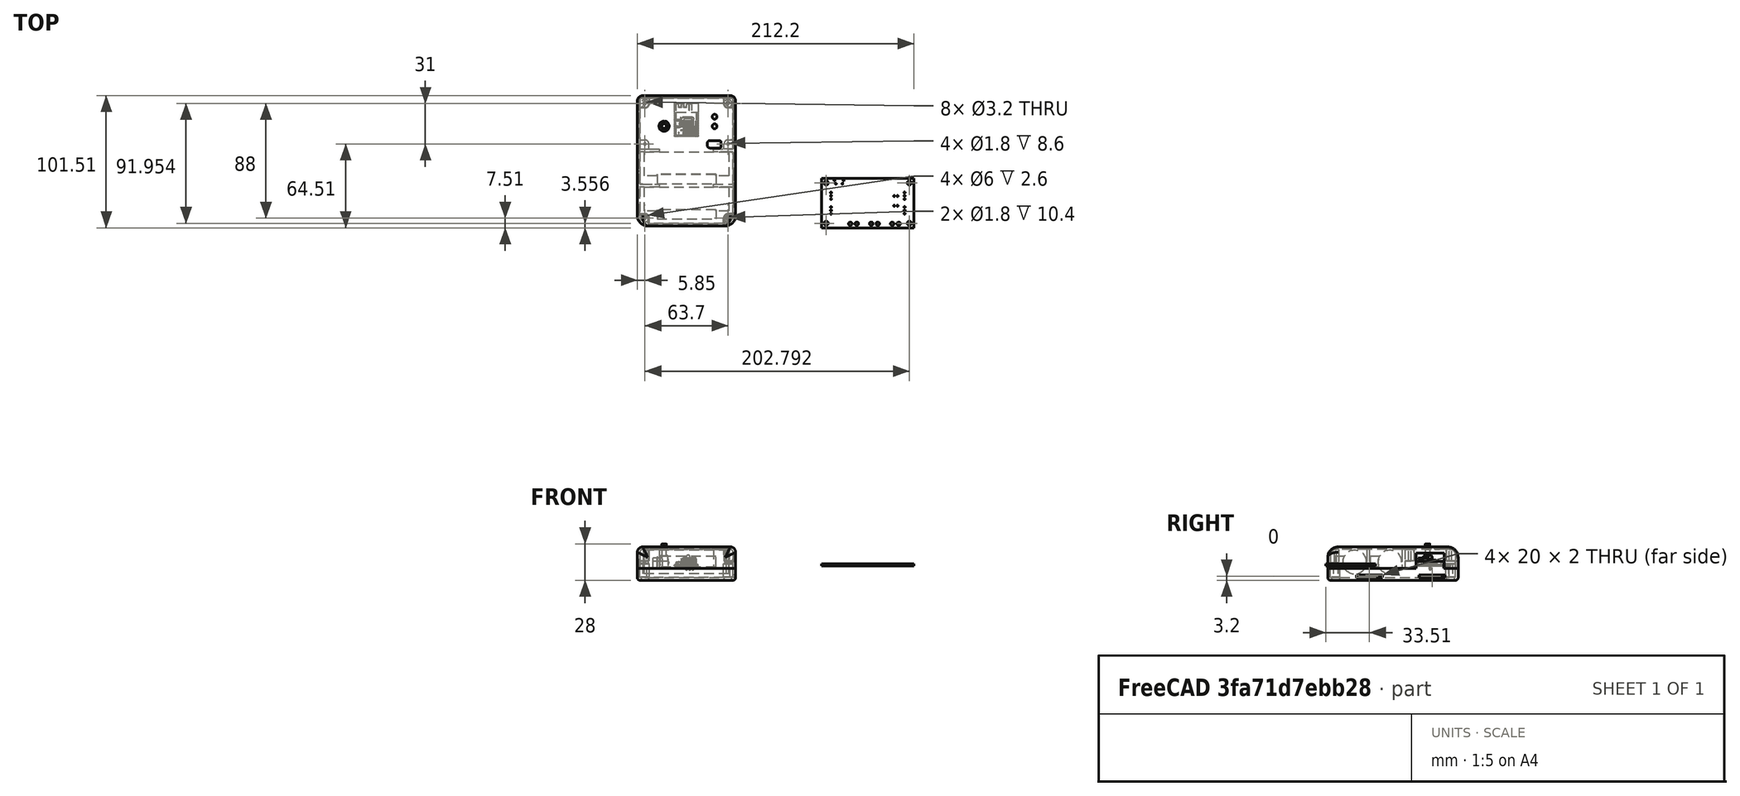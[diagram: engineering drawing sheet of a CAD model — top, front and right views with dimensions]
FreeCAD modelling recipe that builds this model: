
FCSTD DOCUMENT  (FreeCAD 0.21R33694 (Git))
Label: rwled
License: All rights reserved
LicenseURL: http://en.wikipedia.org/wiki/All_rights_reserved
objects: Part::Feature×57, App::Part×44, Sketcher::SketchObject×20, PartDesign::Pad×11, PartDesign::Fillet×11, PartDesign::Pocket×9, PartDesign::Body×4, Part::Part2DObjectPython×1, Mesh::Feature×1, App::DocumentObjectGroup×1
note: 144 computed .brp shape members not serialized (recipe doc carries the construction recipe); baked Part::Feature solids carry a one-line shape summary decoded from their .brp

FEATURE [Part::Feature] Part__Feature  label="SOLID"
  shape: bbox 2 x 1.2 x 0.45 mm, 26 faces (baked)
FEATURE [App::Part] R_0805_2012Metric
  Group = -> [Part__Feature]
  Origin = -> Origin
  Placement = pos=(123.698,-55.352,1.65) rot=(0,0,-1;1.5708rad)
FEATURE [Part::Feature] Part__Feature001  label="SOLID001"
  shape: bbox 7.5 x 4.6 x 2 mm, 40 faces (baked)
FEATURE [App::Part] CP_EIA_7343_20_Kemet_V  label="CP_EIA-7343-20_Kemet-V"
  Group = -> [Part__Feature001]
  Origin = -> Origin045
  Placement = pos=(123.825,-50.8,1.65) rot=(0,0,1;3.14159rad)
FEATURE [Part::Feature] Part__Feature002  label="SOLID002"
  shape: bbox 2.8 x 2.9 x 1.55 mm, 109 faces (baked)
FEATURE [App::Part] SOT_23_5  label="SOT-23-5"
  Group = -> [Part__Feature002]
  Origin = -> Origin046
  Placement = pos=(118.243,-55.372,1.65) rot=(0,0,1;0rad)
FEATURE [Part::Feature] Part__Feature003  label="SOLID003"
  shape: bbox 2 x 2 x 1.05 mm, 118 faces (baked)
FEATURE [App::Part] SOT_363_SC_70_6  label="SOT-363_SC-70-6"
  Group = -> [Part__Feature003]
  Origin = -> Origin047
  Placement = pos=(155.575,-61.468,1.65) rot=(0,0,1;0rad)
FEATURE [Part::Feature] Part__Feature004  label="SOLID004"
  shape: bbox 9.9 x 11.5 x 9.5 mm, 137 faces (baked)
FEATURE [App::Part] JST_XH_S3B_XH_A_1x03_P2_50mm_Horizontal  label="JST_XH_S3B-XH-A_1x03_P2.50mm_Horizontal"
  Group = -> [Part__Feature004]
  Origin = -> Origin048
  Placement = pos=(167.259,-69.048,1.65) rot=(0,0,1;1.5708rad)
FEATURE [Part::Feature] Part__Feature005  label="SOLID005"
  shape: bbox 2 x 1.25 x 1.25 mm, 28 faces (baked)
FEATURE [App::Part] C_0805_2012Metric
  Group = -> [Part__Feature005]
  Origin = -> Origin049
  Placement = pos=(150.368,-55.705,1.65) rot=(0,0,-1;1.5708rad)
FEATURE [Part::Feature] Part__Feature006  label="SOLID006"
  shape: bbox 9.9 x 11.5 x 9.5 mm, 137 faces (baked)
FEATURE [App::Part] JST_XH_S3B_XH_A_1x03_P2_50mm_Horizontal001  label="JST_XH_S3B-XH-A_1x03_P2.50mm_Horizontal001"
  Group = -> [Part__Feature006]
  Origin = -> Origin050
  Placement = pos=(110.892,-64.048,1.65) rot=(0,0,-1;1.5708rad)
FEATURE [Part::Feature] Part__Feature007  label="SOLID007"
  shape: bbox 2 x 1.25 x 1.25 mm, 28 faces (baked)
FEATURE [App::Part] C_0805_2012Metric001
  Group = -> [Part__Feature007]
  Origin = -> Origin051
  Placement = pos=(128.016,-55.372,1.65) rot=(0,0,-1;1.5708rad)
FEATURE [Part::Feature] Part__Feature008  label="SOLID008"
  shape: bbox 18 x 25.5 x 3.1 mm, 751 faces (baked)
FEATURE [App::Part] ESP32_WROOM_32  label="ESP32-WROOM-32"
  Group = -> [Part__Feature008]
  Origin = -> Origin052
  Placement = pos=(139.237,-57.805,1.65) rot=(0,0,1;0rad)
FEATURE [Part::Feature] Part__Feature009  label="SOLID009"
  shape: bbox 2.5 x 2 x 0.78 mm, 48 faces (baked)
FEATURE [App::Part] Bosch_LGA_8_2x2_5mm_P0_65mm_ClockwisePinNumbering  label="Bosch_LGA-8_2x2.5mm_P0.65mm_ClockwisePinNumbering"
  Group = -> [Part__Feature009]
  Origin = -> Origin053
  Placement = pos=(154.394,-55.667,1.65) rot=(0,0,-1;1.5708rad)
FEATURE [Part::Feature] Part__Feature010  label="SOLID010"
  shape: bbox 3.4 x 3.8 x 10.8 mm, 16 faces (baked)
FEATURE [App::Part] LED_D3_0mm  label="LED_D3.0mm"
  Group = -> [Part__Feature010]
  Origin = -> Origin054
  Placement = pos=(159.385,-55.6006,1.65) rot=(0,0,1;0rad)
FEATURE [Part::Feature] Part__Feature011  label="SOLID011"
  shape: bbox 9.9 x 11.5 x 9.5 mm, 137 faces (baked)
FEATURE [App::Part] JST_XH_S3B_XH_A_1x03_P2_50mm_Horizontal002  label="JST_XH_S3B-XH-A_1x03_P2.50mm_Horizontal002"
  Group = -> [Part__Feature011]
  Origin = -> Origin055
  Placement = pos=(167.259,-57.86,1.65) rot=(0,0,1;1.5708rad)
FEATURE [Part::Feature] Part__Feature012  label="SOLID012"
  shape: bbox 2 x 1.25 x 1.25 mm, 28 faces (baked)
FEATURE [App::Part] C_0805_2012Metric002
  Group = -> [Part__Feature012]
  Origin = -> Origin056
  Placement = pos=(121.539,-55.372,1.65) rot=(0,0,-1;1.5708rad)
FEATURE [Part::Feature] Part__Feature013  label="SOLID013"
  shape: bbox 9.9 x 11.5 x 9.5 mm, 137 faces (baked)
FEATURE [App::Part] JST_XH_S3B_XH_A_1x03_P2_50mm_Horizontal003  label="JST_XH_S3B-XH-A_1x03_P2.50mm_Horizontal003"
  Group = -> [Part__Feature013]
  Origin = -> Origin057
  Placement = pos=(110.892,-52.86,1.65) rot=(0,0,-1;1.5708rad)
FEATURE [Part::Feature] Part__Feature014  label="SOLID014"
  shape: bbox 3.4 x 3.8 x 10.8 mm, 16 faces (baked)
FEATURE [App::Part] LED_D3_0mm001  label="LED_D3.0mm001"
  Group = -> [Part__Feature014]
  Origin = -> Origin058
  Placement = pos=(159.385,-62.9901,1.65) rot=(0,0,1;0rad)
FEATURE [Part::Feature] Part__Feature015  label="SOLID015"
  shape: bbox 3.2 x 1.6 x 0.55 mm, 26 faces (baked)
FEATURE [App::Part] R_1206_3216Metric
  Group = -> [Part__Feature015]
  Origin = -> Origin059
  Placement = pos=(160.579,-59.4595,1.65) rot=(0,0,1;0rad)
FEATURE [Part::Feature] Part__Feature016  label="SOLID016"
  shape: bbox 2 x 1.25 x 1.25 mm, 28 faces (baked)
FEATURE [App::Part] C_0805_2012Metric003
  Group = -> [Part__Feature016]
  Origin = -> Origin060
  Placement = pos=(119.507,-58.293,1.65) rot=(0,0,1;0rad)
FEATURE [Part::Feature] Part__Feature017  label="SOLID017"
  shape: bbox 2 x 1.2 x 0.45 mm, 26 faces (baked)
FEATURE [App::Part] R_0805_2012Metric001
  Group = -> [Part__Feature017]
  Origin = -> Origin061
  Placement = pos=(125.862,-55.352,1.65) rot=(0,0,-1;1.5708rad)
FEATURE [Part::Feature] Part__Feature018  label="SOLID018"
  shape: bbox 3.2 x 1.6 x 0.55 mm, 26 faces (baked)
FEATURE [App::Part] R_1206_3216Metric001
  Group = -> [Part__Feature018]
  Origin = -> Origin062
  Placement = pos=(160.579,-52.07,1.65) rot=(0,0,1;0rad)
FEATURE [Part::Feature] Part__Feature019  label="SOLID019"
  shape: bbox 2 x 1.2 x 0.45 mm, 26 faces (baked)
FEATURE [App::Part] R_0805_2012Metric002
  Group = -> [Part__Feature019]
  Origin = -> Origin063
  Placement = pos=(136.779,-52.324,-0.05) rot=(0.707107,-0.707107,0;3.14159rad)
FEATURE [Part::Feature] Part__Feature020  label="SOLID020"
  shape: bbox 2 x 1.2 x 0.45 mm, 26 faces (baked)
FEATURE [App::Part] R_0805_2012Metric003
  Group = -> [Part__Feature020]
  Origin = -> Origin064
  Placement = pos=(128.88,-57.967,-0.05) rot=(0.707107,-0.707107,0;3.14159rad)
FEATURE [Part::Feature] Part__Feature021  label="SOLID021"
  shape: bbox 4 x 4 x 0.77 mm, 158 faces (baked)
FEATURE [App::Part] QFN_24_1EP_4x4mm_P0_5mm_EP2_6x2_6mm  label="QFN-24-1EP_4x4mm_P0.5mm_EP2.6x2.6mm"
  Group = -> [Part__Feature021]
  Origin = -> Origin065
  Placement = pos=(126.397,-49.042,-0.05) rot=(1,0,0;3.14159rad)
FEATURE [Part::Feature] Part__Feature022  label="SOLID022"
  shape: bbox 5 x 2.7 x 2.22 mm, 41 faces (baked)
FEATURE [App::Part] D_SMA
  Group = -> [Part__Feature022]
  Origin = -> Origin066
  Placement = pos=(155.467,-71.628,-0.05) rot=(1,0,0;3.14159rad)
FEATURE [Part::Feature] Part__Feature023  label="SOLID023"
  shape: bbox 5 x 2.7 x 2.22 mm, 41 faces (baked)
FEATURE [App::Part] D_SMA001
  Group = -> [Part__Feature023]
  Origin = -> Origin067
  Placement = pos=(132.62,-71.628,-0.05) rot=(1,0,0;3.14159rad)
FEATURE [Part::Feature] Part__Feature024  label="SOLID024"
  shape: bbox 2.5 x 1.25 x 1.1 mm, 67 faces (baked)
FEATURE [App::Part] D_SOD_323  label="D_SOD-323"
  Group = -> [Part__Feature024]
  Origin = -> Origin068
  Placement = pos=(121.869,-55.1348,-0.05) rot=(0.707107,-0.707107,0;3.14159rad)
FEATURE [Part::Feature] Part__Feature025  label="SOLID025"
  shape: bbox 2 x 1.2 x 0.45 mm, 26 faces (baked)
FEATURE [App::Part] R_0805_2012Metric004
  Group = -> [Part__Feature025]
  Origin = -> Origin069
  Placement = pos=(132.612,-45.593,-0.05) rot=(0,1,0;3.14159rad)
FEATURE [Part::Feature] Part__Feature026  label="COMPOUND"
  shape: bbox 9.25 x 10 x 4.4 mm, 13 faces (baked)
FEATURE [Part::Feature] Part__Feature027  label="COMPOUND001"
  shape: bbox 7.55 x 10 x 1.27 mm, 12 faces (baked)
FEATURE [Part::Feature] Part__Feature028  label="COMPOUND002"
  shape: bbox 4.95 x 1.24 x 2.95 mm, 22 faces (baked)
FEATURE [Part::Feature] Part__Feature029  label="COMPOUND003"
  shape: bbox 1.3 x 1.24 x 0.5 mm, 10 faces (baked)
FEATURE [Part::Feature] Part__Feature030  label="COMPOUND004"
  shape: bbox 4.95 x 1.24 x 2.95 mm, 22 faces (baked)
FEATURE [App::Part] COMPOUND  label="COMPOUND005"
  Group = -> [Part__Feature026,Part__Feature027,Part__Feature028,Part__Feature029,Part__Feature030]
  Origin = -> Origin070
FEATURE [App::Part] TO_263_2  label="TO-263-2"
  Group = -> [COMPOUND]
  Origin = -> Origin071
  Placement = pos=(144.164,-67.195,-0.05) rot=(0.707107,-0.707107,0;3.14159rad)
FEATURE [Part::Feature] Part__Feature031  label="SOLID026"
  shape: bbox 2 x 1.25 x 1.25 mm, 28 faces (baked)
FEATURE [App::Part] C_0805_2012Metric004
  Group = -> [Part__Feature031]
  Origin = -> Origin072
  Placement = pos=(136.398,-66.421,-0.05) rot=(1,0,0;3.14159rad)
FEATURE [Part::Feature] Part__Feature032  label="SOLID027"
  shape: bbox 2 x 1.2 x 0.45 mm, 26 faces (baked)
FEATURE [App::Part] R_0805_2012Metric005
  Group = -> [Part__Feature032]
  Origin = -> Origin073
  Placement = pos=(125.476,-44.577,-0.05) rot=(0,1,0;3.14159rad)
FEATURE [Part::Feature] Part__Feature033  label="SOLID028"
  shape: bbox 2.5 x 1.25 x 1.1 mm, 67 faces (baked)
FEATURE [App::Part] D_SOD_324  label="D_SOD-324"
  Group = -> [Part__Feature033]
  Origin = -> Origin074
  Placement = pos=(120.853,-50.673,-0.05) rot=(0,1,0;3.14159rad)
FEATURE [Part::Feature] Part__Feature034  label="SOLID029"
  shape: bbox 2 x 1.25 x 1.25 mm, 28 faces (baked)
FEATURE [App::Part] C_0805_2012Metric005
  Group = -> [Part__Feature034]
  Origin = -> Origin075
  Placement = pos=(115.824,-51.562,-0.05) rot=(0.707107,-0.707107,0;3.14159rad)
FEATURE [Part::Feature] Part__Feature035  label="SOLID030"
  shape: bbox 2 x 2 x 1.05 mm, 118 faces (baked)
FEATURE [App::Part] SOT_363_SC_70_007  label="SOT-363_SC-70-007"
  Group = -> [Part__Feature035]
  Origin = -> Origin076
  Placement = pos=(133.858,-57.9905,-0.05) rot=(0.707107,-0.707107,0;3.14159rad)
FEATURE [Part::Feature] Part__Feature036  label="SOLID031"
  shape: bbox 2 x 1.2 x 0.45 mm, 26 faces (baked)
FEATURE [App::Part] R_0805_2012Metric006
  Group = -> [Part__Feature036]
  Origin = -> Origin077
  Placement = pos=(142.543,-55.2196,-0.05) rot=(1,0,0;3.14159rad)
FEATURE [Part::Feature] Part__Feature037  label="SOLID032"
  shape: bbox 2 x 1.25 x 1.25 mm, 28 faces (baked)
FEATURE [App::Part] C_0805_2012Metric006
  Group = -> [Part__Feature037]
  Origin = -> Origin078
  Placement = pos=(116.713,-75.504,-0.05) rot=(0.707107,-0.707107,0;3.14159rad)
FEATURE [Part::Feature] Part__Feature038  label="COMPOUND006"
  shape: bbox 9.25 x 10 x 4.4 mm, 13 faces (baked)
FEATURE [Part::Feature] Part__Feature039  label="COMPOUND007"
  shape: bbox 7.55 x 10 x 1.27 mm, 12 faces (baked)
FEATURE [Part::Feature] Part__Feature040  label="COMPOUND008"
  shape: bbox 4.95 x 1.24 x 2.95 mm, 22 faces (baked)
FEATURE [Part::Feature] Part__Feature041  label="COMPOUND009"
  shape: bbox 1.3 x 1.24 x 0.5 mm, 10 faces (baked)
FEATURE [Part::Feature] Part__Feature042  label="COMPOUND010"
  shape: bbox 4.95 x 1.24 x 2.95 mm, 22 faces (baked)
FEATURE [App::Part] COMPOUND001  label="COMPOUND011"
  Group = -> [Part__Feature038,Part__Feature039,Part__Feature040,Part__Feature041,Part__Feature042]
  Origin = -> Origin079
FEATURE [App::Part] TO_263_003  label="TO-263-003"
  Group = -> [COMPOUND001]
  Origin = -> Origin080
  Placement = pos=(121.304,-67.195,-0.05) rot=(0.707107,-0.707107,0;3.14159rad)
FEATURE [Part::Feature] Part__Feature043  label="SOLID033"
  shape: bbox 2 x 1.2 x 0.45 mm, 26 faces (baked)
FEATURE [App::Part] R_0805_2012Metric007
  Group = -> [Part__Feature043]
  Origin = -> Origin081
  Placement = pos=(133.924,-61.214,-0.05) rot=(0,1,0;3.14159rad)
FEATURE [Part::Feature] Part__Feature044  label="SOLID034"
  shape: bbox 2 x 2 x 1.05 mm, 118 faces (baked)
FEATURE [App::Part] SOT_363_SC_70_008  label="SOT-363_SC-70-008"
  Group = -> [Part__Feature044]
  Origin = -> Origin082
  Placement = pos=(132.522,-52.593,-0.05) rot=(0,1,0;3.14159rad)
FEATURE [Part::Feature] Part__Feature045  label="SOLID035"
  shape: bbox 2 x 1.2 x 0.45 mm, 26 faces (baked)
FEATURE [App::Part] R_0805_2012Metric008
  Group = -> [Part__Feature045]
  Origin = -> Origin083
  Placement = pos=(132.612,-49.911,-0.05) rot=(0,1,0;3.14159rad)
FEATURE [Part::Feature] Part__Feature046  label="SOLID036"
  shape: bbox 2.5 x 1.25 x 1.1 mm, 67 faces (baked)
FEATURE [App::Part] D_SOD_325  label="D_SOD-325"
  Group = -> [Part__Feature046]
  Origin = -> Origin084
  Placement = pos=(142.636,-52.8066,-0.05) rot=(1,0,0;3.14159rad)
FEATURE [Part::Feature] Part__Feature047  label="SOLID037"
  shape: bbox 2 x 1.2 x 0.45 mm, 26 faces (baked)
FEATURE [App::Part] R_0805_2012Metric009
  Group = -> [Part__Feature047]
  Origin = -> Origin085
  Placement = pos=(132.612,-47.879,-0.05) rot=(0,1,0;3.14159rad)
FEATURE [Part::Feature] Part__Feature048  label="rwled-ctrl PCB"
  shape: bbox 70.87 x 38.1 x 1.6 mm, 74 faces (baked)
FEATURE [App::Part] rwled_ctrl_1  label="rwled-ctrl 1"
  Group = -> [R_0805_2012Metric,CP_EIA_7343_20_Kemet_V,SOT_23_5,SOT_363_SC_70_6,JST_XH_S3B_XH_A_1x03_P2_50mm_Horizontal,C_0805_2012Metric,JST_XH_S3B_XH_A_1x03_P2_50mm_Horizontal001,C_0805_2012Metric001,ESP32_WROOM_32,Bosch_LGA_8_2x2_5mm_P0_65mm_ClockwisePinNumbering,LED_D3_0mm,JST_XH_S3B_XH_A_1x03_P2_50mm_Horizontal002,C_0805_2012Metric002,JST_XH_S3B_XH_A_1x03_P2_50mm_Horizontal003,LED_D3_0mm001,+26 more]
  Origin = -> Origin086
  Placement = pos=(-139.065,60.96,2) rot=(0,0,1;0rad)
FEATURE [Sketcher::SketchObject] Sketch
  FullyConstrained = true
  MapMode = 5
  Support = -> [XY_Plane043]
  sketch-geometry (4):
    g0: LineSegment StartX=-37.7 StartY=21.5 StartZ=0 EndX=37.7 EndY=21.5 EndZ=0
    g1: LineSegment StartX=37.7 StartY=21.5 StartZ=0 EndX=37.7 EndY=-78.5 EndZ=0
    g2: LineSegment StartX=37.7 StartY=-78.5 StartZ=0 EndX=-37.7 EndY=-78.5 EndZ=0
    g3: LineSegment StartX=-37.7 StartY=-78.5 StartZ=0 EndX=-37.7 EndY=21.5 EndZ=0
  constraints (11):
    c: Coincident(g0,g1)
    c: Coincident(g1,g2)
    c: Coincident(g2,g3)
    c: Coincident(g3,g0)
    c: Horizontal(g2)
    c: Vertical(g1)
    c: Vertical(g3)
    c: Symmetric(g0,g0,g-2)
    c: Distance(g0) = 75.4
    c: Distance(g0,g-1) = 21.5
    c: DistanceY(g3,g3) = 100
FEATURE [Part::Feature] Part__Feature049  label="Micro USB-B Female 5Pin SMD"
  shape: bbox 0.3 x 1.55 x 4.2 mm, 15 faces (baked)
FEATURE [Part::Feature] Part__Feature050  label="Micro USB-B Female 5Pin SMD001"
  shape: bbox 0.3 x 1.55 x 4.2 mm, 15 faces (baked)
FEATURE [Part::Feature] Part__Feature051  label="Micro USB-B Female 5Pin SMD002"
  shape: bbox 0.3 x 1.55 x 4.2 mm, 15 faces (baked)
FEATURE [Part::Feature] Part__Feature052  label="Micro USB-B Female 5Pin SMD003"
  shape: bbox 0.3 x 1.55 x 4.2 mm, 15 faces (baked)
FEATURE [Part::Feature] Part__Feature053  label="Micro USB-B Female 5Pin SMD004"
  shape: bbox 0.3 x 1.55 x 4.2 mm, 15 faces (baked)
FEATURE [Part::Feature] Part__Feature054  label="Micro USB-B Female 5Pin SMD005"
  shape: bbox 6.9 x 2.4 x 4.15 mm, 176 faces (baked)
FEATURE [Part::Feature] Part__Feature055  label="Micro USB-B Female 5Pin SMD006"
  shape: bbox 8.172 x 3.786 x 5.619 mm, 257 faces (baked)
FEATURE [App::Part] Micro_USB_B_Female_5Pin_SMD  label="Micro USB-B Female 5Pin SMD007"
  Group = -> [Part__Feature049,Part__Feature050,Part__Feature051,Part__Feature052,Part__Feature053,Part__Feature054,Part__Feature055]
  Origin = -> Origin087
  Placement = pos=(-22,14.6,4.85) rot=(0,1,1;3.14159rad)
FEATURE [Part::Feature] Part__Feature056  label="SW_PUSH_6mm_h13mm"
  Placement = pos=(-20.29,0.35,4) rot=(0,0,1;0rad)
  shape: bbox 7.174 x 6 x 16.5 mm, 105 faces (baked)
FEATURE [PartDesign::Pad] Pad
  Direction = (0,0,1)
  Length = 16.6
  Length2 = 10
  Profile = -> Sketch
  ReferenceAxis = -> Sketch [N_Axis]
  Type = 0
FEATURE [Sketcher::SketchObject] Sketch001
  FullyConstrained = true
  MapMode = 5
  Placement = pos=(0,0,0) rot=(0.57735,0.57735,0.57735;2.0944rad)
  Support = -> [YZ_Plane088]
  sketch-geometry (1):
    g0: Circle CenterX=9.1 CenterY=0 CenterZ=0 NormalX=0 NormalY=0 NormalZ=1 AngleXU=0 Radius=9.1
  constraints (3):
    c: PointOnObject(g0,g-1)
    c: Distance(g-1,g0) = 9.1
    c: PointOnObject(g-1,g0)
FEATURE [PartDesign::Pad] Pad001
  Direction = (1,-2e-16,3e-16)
  Length = 65
  Length2 = 10
  Placement = pos=(0,0,0) rot=(0.57735,0.57735,0.57735;2.0944rad)
  Profile = -> Sketch001
  ReferenceAxis = -> Sketch001 [N_Axis]
  Type = 0
FEATURE [Sketcher::SketchObject] Sketch002
  FullyConstrained = false
  MapMode = 5
  Placement = pos=(0,0,0) rot=(1,0,0;1.5708rad)
  Support = -> [XZ_Plane088]
  sketch-geometry (4):
    g0: LineSegment StartX=10 StartY=-3.77048 StartZ=0 EndX=55 EndY=-3.77048 EndZ=0
    g1: LineSegment StartX=55 StartY=-3.77048 StartZ=0 EndX=55 EndY=4.22952 EndZ=0
    g2: LineSegment StartX=55 StartY=4.22952 StartZ=0 EndX=10 EndY=4.22952 EndZ=0
    g3: LineSegment StartX=10 StartY=4.22952 StartZ=0 EndX=10 EndY=-3.77048 EndZ=0
  constraints (11):
    c: Coincident(g0,g1)
    c: Coincident(g1,g2)
    c: Coincident(g2,g3)
    c: Coincident(g3,g0)
    c: Horizontal(g0)
    c: Horizontal(g2)
    c: Vertical(g1)
    c: Vertical(g3)
    c: DistanceX(g-1,g0) = 10
    c: DistanceX(g2,g2) = 45
    c: DistanceY(g3,g3) = 8
FEATURE [PartDesign::Pad] Pad002
  BaseFeature = -> Pad001
  Direction = (0,-1,2e-16)
  Length = 6
  Length2 = 10
  Placement = pos=(0,0,0) rot=(0.57735,0.57735,0.57735;2.0944rad)
  Profile = -> Sketch002
  ReferenceAxis = -> Sketch002 [N_Axis]
  Type = 4
FEATURE [PartDesign::Body] Body001  label="accum-a"
  Group = -> [Sketch001,Pad001,Sketch002,Pad002]
  Origin = -> Origin088
  Placement = pos=(-32.5,-40,3) rot=(0,0,1;0rad)
  Tip = -> Pad002
FEATURE [Sketcher::SketchObject] Sketch003
  FullyConstrained = true
  MapMode = 5
  Placement = pos=(0,0,0) rot=(0.57735,0.57735,0.57735;2.0944rad)
  Support = -> [YZ_Plane090]
  sketch-geometry (1):
    g0: Circle CenterX=9.1 CenterY=0 CenterZ=0 NormalX=0 NormalY=0 NormalZ=1 AngleXU=0 Radius=9.1
  constraints (3):
    c: PointOnObject(g0,g-1)
    c: Distance(g-1,g0) = 9.1
    c: PointOnObject(g-1,g0)
FEATURE [PartDesign::Pad] Pad003
  Direction = (1,-2e-16,3e-16)
  Length = 65
  Length2 = 10
  Placement = pos=(0,0,0) rot=(0.57735,0.57735,0.57735;2.0944rad)
  Profile = -> Sketch003
  ReferenceAxis = -> Sketch003 [N_Axis]
  Type = 0
FEATURE [Sketcher::SketchObject] Sketch004
  FullyConstrained = false
  MapMode = 5
  Placement = pos=(0,0,0) rot=(1,0,0;1.5708rad)
  Support = -> [XZ_Plane090]
  sketch-geometry (4):
    g0: LineSegment StartX=10 StartY=-3.77048 StartZ=0 EndX=55 EndY=-3.77048 EndZ=0
    g1: LineSegment StartX=55 StartY=-3.77048 StartZ=0 EndX=55 EndY=4.22952 EndZ=0
    g2: LineSegment StartX=55 StartY=4.22952 StartZ=0 EndX=10 EndY=4.22952 EndZ=0
    g3: LineSegment StartX=10 StartY=4.22952 StartZ=0 EndX=10 EndY=-3.77048 EndZ=0
  constraints (11):
    c: Coincident(g0,g1)
    c: Coincident(g1,g2)
    c: Coincident(g2,g3)
    c: Coincident(g3,g0)
    c: Horizontal(g0)
    c: Horizontal(g2)
    c: Vertical(g1)
    c: Vertical(g3)
    c: DistanceX(g-1,g0) = 10
    c: DistanceX(g2,g2) = 45
    c: DistanceY(g3,g3) = 8
FEATURE [PartDesign::Pad] Pad004
  BaseFeature = -> Pad003
  Direction = (0,-1,2e-16)
  Length = 6
  Length2 = 10
  Placement = pos=(0,0,0) rot=(0.57735,0.57735,0.57735;2.0944rad)
  Profile = -> Sketch004
  ReferenceAxis = -> Sketch004 [N_Axis]
  Type = 4
FEATURE [PartDesign::Body] Body003  label="accum-b"
  Group = -> [Sketch003,Pad003,Sketch004,Pad004]
  Origin = -> Origin090
  Placement = pos=(-32.5,-67,3) rot=(0,0,1;0rad)
  Tip = -> Pad004
FEATURE [Sketcher::SketchObject] Sketch005
  ExternalGeometry = -> [Pad]
  FullyConstrained = true
  MapMode = 5
  Placement = pos=(0,0,0) rot=(1,0,0;3.14159rad)
  Support = -> [Pad]
  sketch-geometry (4):
    g0: LineSegment StartX=-35.7 StartY=76.5 StartZ=0 EndX=35.7 EndY=76.5 EndZ=0
    g1: LineSegment StartX=35.7 StartY=76.5 StartZ=0 EndX=35.7 EndY=-19.5 EndZ=0
    g2: LineSegment StartX=35.7 StartY=-19.5 StartZ=0 EndX=-35.7 EndY=-19.5 EndZ=0
    g3: LineSegment StartX=-35.7 StartY=-19.5 StartZ=0 EndX=-35.7 EndY=76.5 EndZ=0
  constraints (11):
    c: Coincident(g0,g1)
    c: Coincident(g1,g2)
    c: Coincident(g2,g3)
    c: Coincident(g3,g0)
    c: Horizontal(g2)
    c: Vertical(g1)
    c: Vertical(g3)
    c: DistanceX(g0,g0) = 71.4
    c: DistanceY(g3,g3) = 96
    c: Symmetric(g0,g0,g-2)
    c: DistanceY(g0,g-3) = 2
FEATURE [PartDesign::Pocket] Pocket
  BaseFeature = -> Pad
  Direction = (0,0,1)
  Length = 14.6
  Length2 = 5
  Profile = -> Sketch005
  ReferenceAxis = -> Sketch005 [N_Axis]
  Type = 0
FEATURE [Sketcher::SketchObject] Sketch006
  FullyConstrained = true
  MapMode = 5
  Placement = pos=(37.7,0,0) rot=(0.57735,0.57735,0.57735;2.0944rad)
  Support = -> [Pocket]
  sketch-geometry (4):
    g0: LineSegment StartX=-10.8 StartY=12 StartZ=0 EndX=10.8 EndY=12 EndZ=0
    g1: LineSegment StartX=10.8 StartY=12 StartZ=0 EndX=10.8 EndY=0 EndZ=0
    g2: LineSegment StartX=10.8 StartY=0 StartZ=0 EndX=-10.8 EndY=0 EndZ=0
    g3: LineSegment StartX=-10.8 StartY=0 StartZ=0 EndX=-10.8 EndY=12 EndZ=0
  constraints (12):
    c: Coincident(g0,g1)
    c: Coincident(g1,g2)
    c: Coincident(g2,g3)
    c: Coincident(g3,g0)
    c: Horizontal(g0)
    c: Horizontal(g2)
    c: Vertical(g1)
    c: Vertical(g3)
    c: DistanceX(g0,g0) = 21.6
    c: DistanceY(g3,g3) = 12
    c: Distance(g2,g-2) = 10.8
    c: PointOnObject(g-1,g2)
FEATURE [PartDesign::Pocket] Pocket001  label="Отверстие разъёмы справа"
  BaseFeature = -> Pocket
  Direction = (-1,0,0)
  Length = 2
  Length2 = 5
  Profile = -> Sketch006
  ReferenceAxis = -> Sketch006 [N_Axis]
  Type = 0
FEATURE [Sketcher::SketchObject] Sketch007
  FullyConstrained = true
  MapMode = 5
  Placement = pos=(-37.7,0,0) rot=(0.57735,-0.57735,-0.57735;2.0944rad)
  Support = -> [Pocket]
  sketch-geometry (4):
    g0: LineSegment StartX=-10.8 StartY=12 StartZ=0 EndX=10.8 EndY=12 EndZ=0
    g1: LineSegment StartX=10.8 StartY=12 StartZ=0 EndX=10.8 EndY=0 EndZ=0
    g2: LineSegment StartX=10.8 StartY=0 StartZ=0 EndX=-10.8 EndY=0 EndZ=0
    g3: LineSegment StartX=-10.8 StartY=0 StartZ=0 EndX=-10.8 EndY=12 EndZ=0
  constraints (12):
    c: Coincident(g0,g1)
    c: Coincident(g1,g2)
    c: Coincident(g2,g3)
    c: Coincident(g3,g0)
    c: Horizontal(g0)
    c: Horizontal(g2)
    c: Vertical(g1)
    c: Vertical(g3)
    c: DistanceX(g0,g0) = 21.6
    c: DistanceY(g3,g3) = 12
    c: Distance(g1,g-2) = 10.8
    c: PointOnObject(g-1,g2)
FEATURE [PartDesign::Pocket] Pocket002  label="Отверстие разъёмы слева"
  BaseFeature = -> Pocket001
  Direction = (1,0,0)
  Length = 2
  Length2 = 5
  Profile = -> Sketch007
  ReferenceAxis = -> Sketch007 [N_Axis]
  Type = 2
FEATURE [Sketcher::SketchObject] Sketch008
  ExternalGeometry = -> [Pocket]
  FullyConstrained = true
  MapMode = 5
  Placement = pos=(0,21.5,0) rot=(0,0.707107,0.707107;3.14159rad)
  Support = -> [Pocket]
  sketch-geometry (4):
    g0: LineSegment StartX=18.2 StartY=8.2 StartZ=0 EndX=25.8 EndY=8.2 EndZ=0
    g1: LineSegment StartX=25.8 StartY=8.2 StartZ=0 EndX=25.8 EndY=0 EndZ=0
    g2: LineSegment StartX=25.8 StartY=0 StartZ=0 EndX=18.2 EndY=0 EndZ=0
    g3: LineSegment StartX=18.2 StartY=0 StartZ=0 EndX=18.2 EndY=8.2 EndZ=0
  constraints (12):
    c: Coincident(g0,g1)
    c: Coincident(g1,g2)
    c: Coincident(g2,g3)
    c: Coincident(g3,g0)
    c: Horizontal(g0)
    c: Horizontal(g2)
    c: Vertical(g1)
    c: Vertical(g3)
    c: PointOnObject(g1,g-1)
    c: Distance(g-3,g1) = 11.9
    c: DistanceX(g0,g0) = 7.6
    c: DistanceY(g3,g3) = 8.2
FEATURE [PartDesign::Pocket] Pocket003  label="Отверстие usb"
  BaseFeature = -> Pocket002
  Direction = (0,-1,2e-16)
  Length = 2
  Length2 = 5
  Profile = -> Sketch008
  ReferenceAxis = -> Sketch008 [N_Axis]
  Type = 0
FEATURE [Sketcher::SketchObject] Sketch009
  FullyConstrained = false
  MapMode = 5
  Placement = pos=(0,0,16.6) rot=(0,0,1;0rad)
  Support = -> [Pocket]
  sketch-geometry (10):
    g0: Circle CenterX=21.6019 CenterY=-2.03184 CenterZ=0 NormalX=0 NormalY=0 NormalZ=1 AngleXU=0 Radius=1.85
    g1: Circle CenterX=21.5972 CenterY=5.35282 CenterZ=0 NormalX=0 NormalY=0 NormalZ=1 AngleXU=0 Radius=1.85
    g2: LineSegment StartX=15.8257 StartY=-15.3377 StartZ=0 EndX=15.8257 EndY=-16.3217 EndZ=0
    g3: LineSegment StartX=26.545 StartY=-14.2196 StartZ=0 EndX=26.545 EndY=-17.3559 EndZ=0
    g4: LineSegment StartX=17.9219 StartY=-13.0027 StartZ=0 EndX=25.2742 EndY=-13.0027 EndZ=0
    g5: LineSegment StartX=17.897 StartY=-18.6636 StartZ=0 EndX=25.2824 EndY=-18.6636 EndZ=0
    g6: ArcOfCircle CenterX=18.1168 CenterY=-15.2861 CenterZ=0 NormalX=0 NormalY=0 NormalZ=1 AngleXU=0 Radius=2.29165 StartAngle=1.65595 EndAngle=3.16413
    g7: ArcOfCircle CenterX=18.1087 CenterY=-16.3895 CenterZ=0 NormalX=0 NormalY=0 NormalZ=1 AngleXU=0 Radius=2.28395 StartAngle=3.11191 EndAngle=4.61961
    g8: ArcOfCircle CenterX=25.295 CenterY=-14.253 CenterZ=0 NormalX=0 NormalY=0 NormalZ=1 AngleXU=0 Radius=1.25044 StartAngle=0.026699 EndAngle=1.58738
    g9: ArcOfCircle CenterX=25.2642 CenterY=-17.3827 CenterZ=0 NormalX=0 NormalY=0 NormalZ=1 AngleXU=0 Radius=1.28106 StartAngle=4.7266 EndAngle=6.30404
  constraints (14):
    c: Diameter(g0) = 3.7
    c: Diameter(g1) = 3.7
    c: Vertical(g2)
    c: Vertical(g3)
    c: Horizontal(g4)
    c: Horizontal(g5)
    c: Coincident(g6,g2)
    c: Coincident(g6,g4)
    c: Coincident(g7,g2)
    c: Coincident(g7,g5)
    c: Coincident(g8,g4)
    c: Coincident(g8,g3)
    c: Coincident(g9,g3)
    c: Coincident(g9,g5)
FEATURE [PartDesign::Pocket] Pocket004  label="Отверстия индикация"
  BaseFeature = -> Pocket003
  Direction = (0,0,-1)
  Length = 2
  Length2 = 5
  Profile = -> Sketch009
  ReferenceAxis = -> Sketch009 [N_Axis]
  Type = 0
FEATURE [Sketcher::SketchObject] Sketch010
  FullyConstrained = false
  MapMode = 5
  Placement = pos=(0,0,16.6) rot=(0,0,1;0rad)
  Support = -> [Pocket]
  sketch-geometry (3):
    g0: Circle CenterX=-17.1458 CenterY=-1.90076 CenterZ=0 NormalX=0 NormalY=0 NormalZ=1 AngleXU=0 Radius=3.9
    g1: GeomPoint X=-17.1369 Y=-1.89872 Z=0
    g2: GeomPoint X=-17.1369 Y=-1.89872 Z=0
  constraints (2):
    c: Diameter(g0) = 7.8
    c: Coincident(g2,g1)
FEATURE [Part::Part2DObjectPython] Circle  # Draft 2D object (typed FeaturePython)
  Area = 0.502819
  FirstAngle = 0
  LastAngle = 0
  MakeFace = true
  Placement = pos=(-17.14,-1.9,15) rot=(0,0,1;1.5708rad)
  Radius = 0.400065
FEATURE [PartDesign::Pocket] Pocket005  label="Отверстие кнопка (конус)"
  BaseFeature = -> Pocket004
  Direction = (0,0,-1)
  Length = 2
  Length2 = 5
  Profile = -> Sketch010
  ReferenceAxis = -> Sketch010 [N_Axis]
  TaperAngle = -45
  Type = 0
FEATURE [Sketcher::SketchObject] Sketch011
  ExternalGeometry = -> [Pocket]
  FullyConstrained = false
  MapMode = 5
  Placement = pos=(0,0,14.6) rot=(1,0,0;3.14159rad)
  Support = -> [Pocket]
  sketch-geometry (18):
    g0: LineSegment StartX=-35.7 StartY=46.5 StartZ=0 EndX=-20.7 EndY=46.5 EndZ=0
    g1: LineSegment StartX=-20.7 StartY=46.5 StartZ=0 EndX=-20.7 EndY=48.5 EndZ=0
    g2: LineSegment StartX=-20.7 StartY=48.5 StartZ=0 EndX=-35.7 EndY=48.5 EndZ=0
    g3: LineSegment StartX=-35.7 StartY=48.5 StartZ=0 EndX=-35.7 EndY=46.5 EndZ=0
    g4: LineSegment StartX=-35.7 StartY=19.5 StartZ=0 EndX=-20.7 EndY=19.5 EndZ=0
    g5: LineSegment StartX=-20.7 StartY=19.5 StartZ=0 EndX=-20.7 EndY=21.5 EndZ=0
    g6: LineSegment StartX=-20.7 StartY=21.5 StartZ=0 EndX=-35.7 EndY=21.5 EndZ=0
    g7: LineSegment StartX=-35.7 StartY=21.5 StartZ=0 EndX=-35.7 EndY=19.5 EndZ=0
    g8: LineSegment StartX=35.7 StartY=48.5 StartZ=0 EndX=20.7 EndY=48.5 EndZ=0
    g9: LineSegment StartX=20.7 StartY=48.5 StartZ=0 EndX=20.7 EndY=46.5 EndZ=0
    g10: LineSegment StartX=20.7 StartY=46.5 StartZ=0 EndX=35.7 EndY=46.5 EndZ=0
    g11: LineSegment StartX=35.7 StartY=46.5 StartZ=0 EndX=35.7 EndY=48.5 EndZ=0
    g12: LineSegment StartX=35.7 StartY=21.5 StartZ=0 EndX=20.7 EndY=21.5 EndZ=0
    g13: LineSegment StartX=20.7 StartY=21.5 StartZ=0 EndX=20.7 EndY=19.5 EndZ=0
    g14: LineSegment StartX=20.7 StartY=19.5 StartZ=0 EndX=35.7 EndY=19.5 EndZ=0
    g15: LineSegment StartX=35.7 StartY=19.5 StartZ=0 EndX=35.7 EndY=21.5 EndZ=0
    g16: GeomPoint X=-35.7 Y=47.5 Z=0
    g17: GeomPoint X=35.7 Y=47.5 Z=0
  constraints (48):
    c: Coincident(g0,g1)
    c: Coincident(g1,g2)
    c: Coincident(g2,g3)
    c: Coincident(g3,g0)
    c: Horizontal(g0)
    c: Horizontal(g2)
    c: Vertical(g1)
    c: Vertical(g3)
    c: PointOnObject(g0,g-3)
    c: Coincident(g4,g5)
    c: Coincident(g5,g6)
    c: Coincident(g6,g7)
    c: Coincident(g7,g4)
    c: Horizontal(g4)
    c: Horizontal(g6)
    c: Vertical(g5)
    c: Vertical(g7)
    c: Distance(g4,g5) = 2
    c: Distance(g0,g1) = 2
    c: Distance(g6) = 15
    c: Distance(g0) = 15
    c: Coincident(g8,g9)
    c: Coincident(g9,g10)
    c: Coincident(g10,g11)
    c: Coincident(g11,g8)
    c: Horizontal(g8)
    c: Horizontal(g10)
    c: Vertical(g9)
    c: Vertical(g11)
    c: PointOnObject(g8,g-4)
    c: Coincident(g12,g13)
    c: Coincident(g13,g14)
    c: Coincident(g14,g15)
    c: Coincident(g15,g12)
    c: Horizontal(g12)
    c: Horizontal(g14)
    c: Vertical(g13)
    c: Vertical(g15)
    c: Distance(g9) = 2
    c: Distance(g13) = 2
    c: Distance(g12) = 15
    c: Distance(g10) = 15
    c: Distance(g-3,g4) = 39
    c: Symmetric(g2,g0,g16)
    c: Symmetric(g8,g10,g17)
    c: Distance(g14,g-4) = 39
    c: Distance(g10,g12) = 25
    c: Distance(g0,g6) = 25
FEATURE [PartDesign::Pad] Pad005  label="Перегородки внутр"
  BaseFeature = -> Pocket005
  Direction = (0,0,-1)
  Length = 14.6
  Length2 = 10
  Profile = -> Sketch011
  ReferenceAxis = -> Sketch011 [N_Axis]
  Type = 0
FEATURE [Sketcher::SketchObject] Sketch012
  ExternalGeometry = -> [Pocket]
  FullyConstrained = true
  MapMode = 5
  Placement = pos=(0,0,14.6) rot=(1,0,0;3.14159rad)
  Support = -> [Pocket]
  sketch-geometry (24):
    g0: LineSegment StartX=-35.7 StartY=-12.5 StartZ=0 EndX=-31.85 EndY=-12.5 EndZ=0
    g1: LineSegment StartX=-28.85 StartY=-19.5 StartZ=0 EndX=-28.85 EndY=-15.5 EndZ=0
    g2: ArcOfCircle CenterX=-31.85 CenterY=-15.5 CenterZ=0 NormalX=0 NormalY=0 NormalZ=1 AngleXU=0 Radius=3 StartAngle=1e-16 EndAngle=1.5708
    g3: Circle CenterX=-31.85 CenterY=-15.5 CenterZ=0 NormalX=0 NormalY=0 NormalZ=1 AngleXU=0 Radius=0.9
    g4: LineSegment StartX=-28.85 StartY=-19.5 StartZ=0 EndX=-35.7 EndY=-19.5 EndZ=0
    g5: LineSegment StartX=-35.7 StartY=-12.5 StartZ=0 EndX=-35.7 EndY=-19.5 EndZ=0
    g6: Circle CenterX=31.85 CenterY=-15.5 CenterZ=0 NormalX=0 NormalY=0 NormalZ=1 AngleXU=0 Radius=0.9
    g7: LineSegment StartX=28.85 StartY=-19.5 StartZ=0 EndX=28.85 EndY=-15.5 EndZ=0
    g8: LineSegment StartX=35.7 StartY=-12.5 StartZ=0 EndX=31.85 EndY=-12.5 EndZ=0
    g9: ArcOfCircle CenterX=31.85 CenterY=-15.5 CenterZ=0 NormalX=0 NormalY=0 NormalZ=1 AngleXU=0 Radius=3 StartAngle=1.5708 EndAngle=3.14159
    g10: LineSegment StartX=35.7 StartY=-12.5 StartZ=0 EndX=35.7 EndY=-19.5 EndZ=0
    g11: LineSegment StartX=28.85 StartY=-19.5 StartZ=0 EndX=35.7 EndY=-19.5 EndZ=0
    g12: LineSegment StartX=-35.7 StartY=12.5 StartZ=0 EndX=-35.7 EndY=19.5 EndZ=0
    g13: LineSegment StartX=-35.7 StartY=19.5 StartZ=0 EndX=-28.85 EndY=19.5 EndZ=0
    g14: LineSegment StartX=-35.7 StartY=12.5 StartZ=0 EndX=-31.85 EndY=12.5 EndZ=0
    g15: LineSegment StartX=-28.85 StartY=19.5 StartZ=0 EndX=-28.85 EndY=15.5 EndZ=0
    g16: Circle CenterX=-31.85 CenterY=15.5 CenterZ=0 NormalX=0 NormalY=0 NormalZ=1 AngleXU=0 Radius=0.9
    g17: ArcOfCircle CenterX=-31.85 CenterY=15.5 CenterZ=0 NormalX=0 NormalY=0 NormalZ=1 AngleXU=0 Radius=3 StartAngle=4.71239 EndAngle=6.28319
    g18: LineSegment StartX=31.85 StartY=12.5 StartZ=0 EndX=35.7 EndY=12.5 EndZ=0
    g19: LineSegment StartX=35.7 StartY=12.5 StartZ=0 EndX=35.7 EndY=19.5 EndZ=0
    g20: LineSegment StartX=35.7 StartY=19.5 StartZ=0 EndX=28.85 EndY=19.5 EndZ=0
    g21: LineSegment StartX=28.85 StartY=19.5 StartZ=0 EndX=28.85 EndY=15.5 EndZ=0
    g22: Circle CenterX=31.85 CenterY=15.5 CenterZ=0 NormalX=0 NormalY=0 NormalZ=1 AngleXU=0 Radius=0.9
    g23: ArcOfCircle CenterX=31.85 CenterY=15.5 CenterZ=0 NormalX=0 NormalY=0 NormalZ=1 AngleXU=0 Radius=3 StartAngle=3.14159 EndAngle=4.71239
  constraints (71):
    c: PointOnObject(g0,g-5)
    c: Horizontal(g0)
    c: PointOnObject(g1,g-4)
    c: Vertical(g1)
    c: Coincident(g2,g0)
    c: Coincident(g2,g1)
    c: Distance(g2,g-4) = 4
    c: Distance(g2,g-5) = 3.85
    c: Coincident(g3,g2)
    c: Diameter(g3) = 1.8
    c: Distance(g0) = 3.85
    c: Distance(g1) = 4
    c: Coincident(g4,g1)
    c: Coincident(g4,g-5)
    c: Coincident(g5,g0)
    c: Coincident(g5,g4)
    c: Diameter(g2) = 6
    c: Diameter(g6) = 1.8
    c: Distance(g6,g-4) = 4
    c: Distance(g6,g-3) = 3.85
    c: PointOnObject(g7,g-4)
    c: Vertical(g7)
    c: PointOnObject(g8,g-3)
    c: Horizontal(g8)
    c: Distance(g7) = 4
    c: Distance(g8) = 3.85
    c: Coincident(g9,g6)
    c: Coincident(g9,g7)
    c: Coincident(g9,g8)
    c: Diameter(g9) = 6
    c: Coincident(g10,g8)
    c: Coincident(g10,g-4)
    c: Coincident(g11,g7)
    c: Coincident(g11,g10)
    c: PointOnObject(g12,g-5)
    c: PointOnObject(g12,g-5)
    c: Horizontal(g13)
    c: Coincident(g14,g12)
    c: Horizontal(g14)
    c: Coincident(g15,g13)
    c: Vertical(g15)
    c: Distance(g14) = 3.85
    c: Distance(g15) = 4
    c: Diameter(g16) = 1.8
    c: Distance(g16,g12) = 3.85
    c: Distance(g16,g13) = 4
    c: Distance(g13,g4) = 39
    c: Coincident(g17,g16)
    c: Coincident(g17,g15)
    c: Coincident(g17,g14)
    c: Diameter(g17) = 6
    c: Coincident(g13,g12)
    c: PointOnObject(g18,g-3)
    c: Horizontal(g18)
    c: PointOnObject(g19,g18)
    c: PointOnObject(g19,g-3)
    c: Vertical(g19)
    c: Horizontal(g20)
    c: Coincident(g21,g20)
    c: Vertical(g21)
    c: Distance(g18) = 3.85
    c: Distance(g21) = 4
    c: Diameter(g22) = 1.8
    c: Coincident(g20,g19)
    c: Distance(g19,g11) = 39
    c: Distance(g22,g19) = 3.85
    c: Distance(g22,g20) = 4
    c: Coincident(g23,g22)
    c: Coincident(g23,g18)
    c: Coincident(g23,g21)
    c: Diameter(g23) = 6
FEATURE [PartDesign::Pad] Pad006  label="Винты: под платой"
  BaseFeature = -> Pad005
  Direction = (0,0,-1)
  Length = 8.6
  Length2 = 10
  Profile = -> Sketch012
  ReferenceAxis = -> Sketch012 [N_Axis]
  Type = 0
FEATURE [Sketcher::SketchObject] Sketch013
  ExternalGeometry = -> [Pocket]
  FullyConstrained = true
  MapMode = 5
  Placement = pos=(0,0,14.6) rot=(1,0,0;3.14159rad)
  Support = -> [Pocket]
  sketch-geometry (12):
    g0: LineSegment StartX=-35.7 StartY=76.5 StartZ=0 EndX=-29.35 EndY=76.5 EndZ=0
    g1: LineSegment StartX=-35.7 StartY=76.5 StartZ=0 EndX=-35.7 EndY=70 EndZ=0
    g2: LineSegment StartX=-35.7 StartY=70 StartZ=0 EndX=-31.85 EndY=70 EndZ=0
    g3: LineSegment StartX=-29.35 StartY=76.5 StartZ=0 EndX=-29.35 EndY=72.5 EndZ=0
    g4: Circle CenterX=-31.85 CenterY=72.5 CenterZ=0 NormalX=0 NormalY=0 NormalZ=1 AngleXU=0 Radius=0.9
    g5: ArcOfCircle CenterX=-31.85 CenterY=72.5 CenterZ=0 NormalX=0 NormalY=0 NormalZ=1 AngleXU=0 Radius=2.5 StartAngle=4.71239 EndAngle=6.28319
    g6: LineSegment StartX=35.7 StartY=76.5 StartZ=0 EndX=35.7 EndY=70 EndZ=0
    g7: LineSegment StartX=35.7 StartY=76.5 StartZ=0 EndX=29.35 EndY=76.5 EndZ=0
    g8: LineSegment StartX=29.35 StartY=76.5 StartZ=0 EndX=29.35 EndY=72.5 EndZ=0
    g9: LineSegment StartX=35.7 StartY=70 StartZ=0 EndX=31.85 EndY=70 EndZ=0
    g10: Circle CenterX=31.85 CenterY=72.5 CenterZ=0 NormalX=0 NormalY=0 NormalZ=1 AngleXU=0 Radius=0.9
    g11: ArcOfCircle CenterX=31.85 CenterY=72.5 CenterZ=0 NormalX=0 NormalY=0 NormalZ=1 AngleXU=0 Radius=2.5 StartAngle=3.14159 EndAngle=4.71239
  constraints (35):
    c: PointOnObject(g0,g-4)
    c: PointOnObject(g0,g-4)
    c: Coincident(g1,g0)
    c: PointOnObject(g1,g-3)
    c: Vertical(g1)
    c: Coincident(g2,g1)
    c: Horizontal(g2)
    c: Distance(g2) = 3.85
    c: Coincident(g3,g0)
    c: Vertical(g3)
    c: Distance(g3) = 4
    c: Diameter(g4) = 1.8
    c: Distance(g4,g1) = 3.85
    c: Distance(g4,g0) = 4
    c: Coincident(g5,g4)
    c: Coincident(g5,g3)
    c: Coincident(g5,g2)
    c: Diameter(g5) = 5
    c: Coincident(g6,g-5)
    c: PointOnObject(g6,g-5)
    c: Coincident(g7,g6)
    c: PointOnObject(g7,g-4)
    c: Coincident(g8,g7)
    c: Vertical(g8)
    c: Coincident(g9,g6)
    c: Horizontal(g9)
    c: Distance(g9) = 3.85
    c: Distance(g8) = 4
    c: Diameter(g10) = 1.8
    c: Distance(g10,g7) = 4
    c: Distance(g10,g6) = 3.85
    c: Coincident(g11,g10)
    c: Coincident(g11,g9)
    c: Coincident(g11,g8)
    c: Diameter(g11) = 5
FEATURE [PartDesign::Pad] Pad007  label="Винты: низ"
  BaseFeature = -> Pad006
  Direction = (0,0,-1)
  Length = 10.4
  Length2 = 10
  Profile = -> Sketch013
  ReferenceAxis = -> Sketch013 [N_Axis]
  Type = 0
FEATURE [PartDesign::Fillet] Fillet  label="Сглаж: внутр боковые"
  Base = -> Pad007 [Edge62,Edge121,Edge151,Edge143,Edge139,Edge73]
  BaseFeature = -> Pad007
  Radius = 2
  SupportTransform = false
  UseAllEdges = false
FEATURE [PartDesign::Fillet] Fillet001  label="Сглаж: внутр - верх, низ"
  Base = -> Fillet [Edge55,Edge80]
  BaseFeature = -> Fillet
  Radius = 4
  SupportTransform = false
  UseAllEdges = false
FEATURE [PartDesign::Fillet] Fillet002  label="Сглаж: внутр углы верх"
  Base = -> Fillet001 [Edge5,Edge8]
  BaseFeature = -> Fillet001
  Radius = 1
  SupportTransform = false
  UseAllEdges = false
FEATURE [PartDesign::Fillet] Fillet003  label="Сглаж: внутр углы низ"
  Base = -> Fillet002 [Edge244,Edge249]
  BaseFeature = -> Fillet002
  Radius = 6
  SupportTransform = false
  UseAllEdges = false
FEATURE [PartDesign::Fillet] Fillet004  label="Сглаж: внеш - верх, низ, углы низ"
  Base = -> Fillet003 [Edge75,Edge76,Edge71,Edge171]
  BaseFeature = -> Fillet003
  Radius = 8
  SupportTransform = false
  UseAllEdges = false
FEATURE [PartDesign::Fillet] Fillet005  label="Сглаж: внеш - плоскость, бок верх"
  Base = -> Fillet004 [Edge51,Edge55,Edge53,Edge27,Edge25,Edge23,Edge30,Edge46]
  BaseFeature = -> Fillet004
  Radius = 4
  SupportTransform = false
  UseAllEdges = false
FEATURE [PartDesign::Body] Body  label="up"
  Group = -> [Sketch,Pad,Sketch005,Pocket,Sketch006,Pocket001,Sketch007,Pocket002,Sketch008,Pocket003,Sketch009,Pocket004,Sketch010,Pocket005,Sketch011,Pad005,Sketch012,Pad006,Sketch013,Pad007,Fillet,Fillet001,Fillet002,Fillet003,Fillet004,Fillet005]
  Origin = -> Origin043
  Placement = pos=(0,0,-2) rot=(0,0,1;0rad)
  Tip = -> Fillet005
FEATURE [Sketcher::SketchObject] Sketch014
  FullyConstrained = true
  MapMode = 5
  Support = -> [XY_Plane091]
  sketch-geometry (4):
    g0: LineSegment StartX=-37.7 StartY=21.5 StartZ=0 EndX=37.7 EndY=21.5 EndZ=0
    g1: LineSegment StartX=37.7 StartY=21.5 StartZ=0 EndX=37.7 EndY=-78.5 EndZ=0
    g2: LineSegment StartX=37.7 StartY=-78.5 StartZ=0 EndX=-37.7 EndY=-78.5 EndZ=0
    g3: LineSegment StartX=-37.7 StartY=-78.5 StartZ=0 EndX=-37.7 EndY=21.5 EndZ=0
  constraints (11):
    c: Coincident(g0,g1)
    c: Coincident(g1,g2)
    c: Coincident(g2,g3)
    c: Coincident(g3,g0)
    c: Horizontal(g2)
    c: Vertical(g1)
    c: Vertical(g3)
    c: DistanceY(g3,g3) = 100
    c: DistanceX(g0,g0) = 75.4
    c: Symmetric(g0,g0,g-2)
    c: Distance(g0,g-1) = 21.5
FEATURE [PartDesign::Pad] Pad008
  Direction = (0,0,1)
  Length = 9
  Length2 = 10
  Profile = -> Sketch014
  ReferenceAxis = -> Sketch014 [N_Axis]
  Reversed = true
  Type = 0
FEATURE [Sketcher::SketchObject] Sketch015
  ExternalGeometry = -> [Pad008]
  FullyConstrained = true
  MapMode = 5
  Support = -> [Pad008]
  sketch-geometry (4):
    g0: LineSegment StartX=-35.7 StartY=19.5 StartZ=0 EndX=35.7 EndY=19.5 EndZ=0
    g1: LineSegment StartX=35.7 StartY=19.5 StartZ=0 EndX=35.7 EndY=-76.5 EndZ=0
    g2: LineSegment StartX=35.7 StartY=-76.5 StartZ=0 EndX=-35.7 EndY=-76.5 EndZ=0
    g3: LineSegment StartX=-35.7 StartY=-76.5 StartZ=0 EndX=-35.7 EndY=19.5 EndZ=0
  constraints (12):
    c: Coincident(g0,g1)
    c: Coincident(g1,g2)
    c: Coincident(g2,g3)
    c: Coincident(g3,g0)
    c: Horizontal(g0)
    c: Horizontal(g2)
    c: Vertical(g1)
    c: Vertical(g3)
    c: Distance(g0,g-3) = 2
    c: Distance(g0,g-4) = 2
    c: Distance(g0,g-5) = 2
    c: Distance(g1,g-6) = 2
FEATURE [PartDesign::Pocket] Pocket006
  BaseFeature = -> Pad008
  Direction = (0,0,-1)
  Length = 7
  Length2 = 5
  Profile = -> Sketch015
  ReferenceAxis = -> Sketch015 [N_Axis]
  Type = 0
FEATURE [Sketcher::SketchObject] Sketch016
  ExternalGeometry = -> [Pocket006]
  FullyConstrained = true
  MapMode = 5
  Support = -> [Pocket006]
  sketch-geometry (12):
    g0: LineSegment StartX=-37.7 StartY=-10.6 StartZ=0 EndX=-35.7 EndY=-10.6 EndZ=0
    g1: LineSegment StartX=-35.7 StartY=-10.6 StartZ=0 EndX=-35.7 EndY=10.6 EndZ=0
    g2: LineSegment StartX=-35.7 StartY=10.6 StartZ=0 EndX=-37.7 EndY=10.6 EndZ=0
    g3: LineSegment StartX=-37.7 StartY=10.6 StartZ=0 EndX=-37.7 EndY=-10.6 EndZ=0
    g4: LineSegment StartX=35.7 StartY=-10.6 StartZ=0 EndX=37.7 EndY=-10.6 EndZ=0
    g5: LineSegment StartX=37.7 StartY=-10.6 StartZ=0 EndX=37.7 EndY=10.6 EndZ=0
    g6: LineSegment StartX=37.7 StartY=10.6 StartZ=0 EndX=35.7 EndY=10.6 EndZ=0
    g7: LineSegment StartX=35.7 StartY=10.6 StartZ=0 EndX=35.7 EndY=-10.6 EndZ=0
    g8: LineSegment StartX=-25.6 StartY=19.5 StartZ=0 EndX=-18.4 EndY=19.5 EndZ=0
    g9: LineSegment StartX=-18.4 StartY=19.5 StartZ=0 EndX=-18.4 EndY=21.5 EndZ=0
    g10: LineSegment StartX=-18.4 StartY=21.5 StartZ=0 EndX=-25.6 EndY=21.5 EndZ=0
    g11: LineSegment StartX=-25.6 StartY=21.5 StartZ=0 EndX=-25.6 EndY=19.5 EndZ=0
  constraints (36):
    c: Coincident(g0,g1)
    c: Coincident(g1,g2)
    c: Coincident(g2,g3)
    c: Coincident(g3,g0)
    c: Horizontal(g0)
    c: Horizontal(g2)
    c: Vertical(g1)
    c: Vertical(g3)
    c: Coincident(g4,g5)
    c: Coincident(g5,g6)
    c: Coincident(g6,g7)
    c: Coincident(g7,g4)
    c: Horizontal(g4)
    c: Horizontal(g6)
    c: Vertical(g5)
    c: Vertical(g7)
    c: Coincident(g8,g9)
    c: Coincident(g9,g10)
    c: Coincident(g10,g11)
    c: Coincident(g11,g8)
    c: Horizontal(g8)
    c: Horizontal(g10)
    c: Vertical(g9)
    c: Vertical(g11)
    c: PointOnObject(g6,g-8)
    c: PointOnObject(g5,g-7)
    c: PointOnObject(g8,g-4)
    c: PointOnObject(g9,g-6)
    c: PointOnObject(g2,g-5)
    c: PointOnObject(g1,g-3)
    c: DistanceX(g8,g8) = 7.2
    c: Distance(g10,g-6) = 12.1
    c: DistanceY(g3,g3) = 21.2
    c: Distance(g2,g-1) = 10.6
    c: Distance(g6,g-1) = 10.6
    c: DistanceY(g5,g5) = 21.2
FEATURE [PartDesign::Pad] Pad009  label="Прикрытие боковых отверстий"
  BaseFeature = -> Pocket006
  Direction = (0,0,1)
  Length = 5.4
  Length2 = 10
  Profile = -> Sketch016
  ReferenceAxis = -> Sketch016 [N_Axis]
  Type = 0
FEATURE [Sketcher::SketchObject] Sketch017
  ExternalGeometry = -> [Pad009]
  FullyConstrained = true
  MapMode = 5
  Placement = pos=(37.7,0,0) rot=(0.57735,0.57735,0.57735;2.0944rad)
  Support = -> [Pad009]
  sketch-geometry (8):
    g0: LineSegment StartX=-56.5 StartY=-4.8 StartZ=0 EndX=-36.5 EndY=-4.8 EndZ=0
    g1: LineSegment StartX=-36.5 StartY=-4.8 StartZ=0 EndX=-36.5 EndY=-6.8 EndZ=0
    g2: LineSegment StartX=-36.5 StartY=-6.8 StartZ=0 EndX=-56.5 EndY=-6.8 EndZ=0
    g3: LineSegment StartX=-56.5 StartY=-6.8 StartZ=0 EndX=-56.5 EndY=-4.8 EndZ=0
    g4: LineSegment StartX=-8.5 StartY=-4.8 StartZ=0 EndX=11.5 EndY=-4.8 EndZ=0
    g5: LineSegment StartX=11.5 StartY=-4.8 StartZ=0 EndX=11.5 EndY=-6.8 EndZ=0
    g6: LineSegment StartX=11.5 StartY=-6.8 StartZ=0 EndX=-8.5 EndY=-6.8 EndZ=0
    g7: LineSegment StartX=-8.5 StartY=-6.8 StartZ=0 EndX=-8.5 EndY=-4.8 EndZ=0
  constraints (24):
    c: Coincident(g0,g1)
    c: Coincident(g1,g2)
    c: Coincident(g2,g3)
    c: Coincident(g3,g0)
    c: Horizontal(g0)
    c: Horizontal(g2)
    c: Vertical(g1)
    c: Vertical(g3)
    c: Coincident(g4,g5)
    c: Coincident(g5,g6)
    c: Coincident(g6,g7)
    c: Coincident(g7,g4)
    c: Horizontal(g4)
    c: Horizontal(g6)
    c: Vertical(g5)
    c: Vertical(g7)
    c: DistanceX(g0,g0) = 20
    c: DistanceX(g4,g4) = 20
    c: DistanceY(g3,g3) = 2
    c: DistanceY(g7,g7) = 2
    c: DistanceX(g5,g-3) = 10
    c: DistanceX(g1,g6) = 28
    c: DistanceY(g-3,g5) = 2.2
    c: DistanceY(g-3,g1) = 2.2
FEATURE [PartDesign::Pocket] Pocket007  label="Отверстия под ремни"
  BaseFeature = -> Pad009
  Direction = (-1,0,0)
  Length = 5
  Length2 = 5
  Profile = -> Sketch017
  ReferenceAxis = -> Sketch017 [N_Axis]
  Type = 1
FEATURE [Sketcher::SketchObject] Sketch018
  ExternalGeometry = -> [Pocket007]
  FullyConstrained = false
  MapMode = 5
  Placement = pos=(0,0,-7) rot=(0,0,1;0rad)
  Support = -> [Pocket007]
  sketch-geometry (24):
    g0: LineSegment StartX=-31.85 StartY=12.1 StartZ=0 EndX=-35.7 EndY=12.1 EndZ=0
    g1: LineSegment StartX=-35.7 StartY=12.1 StartZ=0 EndX=-35.7 EndY=19.5 EndZ=0
    g2: LineSegment StartX=-35.7 StartY=19.5 StartZ=0 EndX=-28.5639 EndY=19.5 EndZ=0
    g3: LineSegment StartX=-28.5639 StartY=19.5 StartZ=0 EndX=-28.5639 EndY=14.6272 EndZ=0
    g4: Circle CenterX=-31.85 CenterY=15.5 CenterZ=0 NormalX=0 NormalY=0 NormalZ=1 AngleXU=0 Radius=1.6
    g5: ArcOfCircle CenterX=-31.85 CenterY=15.5 CenterZ=0 NormalX=0 NormalY=0 NormalZ=1 AngleXU=0 Radius=3.4 StartAngle=4.71239 EndAngle=6.02359
    g6: LineSegment StartX=28.45 StartY=19.5 StartZ=0 EndX=35.7 EndY=19.5 EndZ=0
    g7: LineSegment StartX=35.7 StartY=19.5 StartZ=0 EndX=35.7 EndY=12.1 EndZ=0
    g8: LineSegment StartX=35.7 StartY=12.1 StartZ=0 EndX=31.85 EndY=12.1 EndZ=0
    g9: LineSegment StartX=28.45 StartY=19.5 StartZ=0 EndX=28.45 EndY=15.5 EndZ=0
    g10: Circle CenterX=31.85 CenterY=15.5 CenterZ=0 NormalX=0 NormalY=0 NormalZ=1 AngleXU=0 Radius=1.6
    g11: ArcOfCircle CenterX=31.85 CenterY=15.5 CenterZ=0 NormalX=0 NormalY=0 NormalZ=1 AngleXU=0 Radius=3.4 StartAngle=3.14159 EndAngle=4.71239
    g12: LineSegment StartX=35.7 StartY=-69.1 StartZ=0 EndX=35.7 EndY=-76.5 EndZ=0
    g13: LineSegment StartX=35.7 StartY=-76.5 StartZ=0 EndX=28.45 EndY=-76.5 EndZ=0
    g14: LineSegment StartX=28.45 StartY=-76.5 StartZ=0 EndX=28.45 EndY=-72.5 EndZ=0
    g15: LineSegment StartX=35.7 StartY=-69.1 StartZ=0 EndX=31.85 EndY=-69.1 EndZ=0
    g16: Circle CenterX=31.85 CenterY=-72.5 CenterZ=0 NormalX=0 NormalY=0 NormalZ=1 AngleXU=0 Radius=1.6
    g17: ArcOfCircle CenterX=31.85 CenterY=-72.5 CenterZ=0 NormalX=0 NormalY=0 NormalZ=1 AngleXU=0 Radius=3.4 StartAngle=1.5708 EndAngle=3.14159
    g18: LineSegment StartX=-35.7 StartY=-76.5 StartZ=0 EndX=-28.45 EndY=-76.5 EndZ=0
    g19: LineSegment StartX=-35.7 StartY=-76.5 StartZ=0 EndX=-35.7 EndY=-69.1 EndZ=0
    g20: LineSegment StartX=-35.7 StartY=-69.1 StartZ=0 EndX=-31.85 EndY=-69.1 EndZ=0
    g21: LineSegment StartX=-28.45 StartY=-76.5 StartZ=0 EndX=-28.45 EndY=-72.5 EndZ=0
    g22: Circle CenterX=-31.85 CenterY=-72.5 CenterZ=0 NormalX=0 NormalY=0 NormalZ=1 AngleXU=0 Radius=1.6
    g23: ArcOfCircle CenterX=-31.85 CenterY=-72.5 CenterZ=0 NormalX=0 NormalY=0 NormalZ=1 AngleXU=0 Radius=3.4 StartAngle=1.9e-15 EndAngle=1.5708
  constraints (65):
    c: PointOnObject(g0,g-5)
    c: Horizontal(g0)
    c: Coincident(g1,g0)
    c: Coincident(g1,g-5)
    c: Coincident(g2,g1)
    c: PointOnObject(g2,g-4)
    c: Vertical(g3)
    c: Diameter(g4) = 3.2
    c: DistanceX(g0,g0) = 3.85
    c: Distance(g4,g1) = 3.85
    c: Distance(g4,g2) = 4
    c: Coincident(g5,g4)
    c: Coincident(g5,g3)
    c: Coincident(g5,g0)
    c: Diameter(g5) = 6.8
    c: PointOnObject(g6,g-4)
    c: Coincident(g6,g-4)
    c: PointOnObject(g7,g-3)
    c: Horizontal(g8)
    c: Coincident(g9,g6)
    c: Vertical(g9)
    c: Diameter(g10) = 3.2
    c: DistanceY(g9,g9) = 4
    c: DistanceX(g8,g8) = 3.85
    c: Distance(g10,g6) = 4
    c: Coincident(g11,g10)
    c: Coincident(g11,g9)
    c: Coincident(g11,g8)
    c: Diameter(g11) = 6.8
    c: PointOnObject(g12,g-3)
    c: Coincident(g12,g-6)
    c: Coincident(g13,g12)
    c: PointOnObject(g13,g-6)
    c: Coincident(g14,g13)
    c: Vertical(g14)
    c: Coincident(g15,g12)
    c: Horizontal(g15)
    c: Diameter(g16) = 3.2
    c: DistanceY(g14,g14) = 4
    c: DistanceX(g15,g15) = 3.85
    c: Distance(g16,g-6) = 4
    c: Distance(g16,g-3) = 3.85
    c: Coincident(g17,g16)
    c: Coincident(g17,g14)
    c: Coincident(g17,g15)
    c: Diameter(g17) = 6.8
    c: Coincident(g18,g-6)
    c: PointOnObject(g18,g-6)
    c: Coincident(g19,g18)
    c: PointOnObject(g19,g-5)
    c: Coincident(g20,g19)
    c: Horizontal(g20)
    c: Coincident(g21,g18)
    c: Vertical(g21)
    c: Diameter(g22) = 3.2
    c: DistanceX(g20,g20) = 3.85
    c: DistanceY(g21,g21) = 4
    c: Distance(g22,g-6) = 4
    c: Distance(g22,g-5) = 3.85
    c: Coincident(g23,g22)
    c: Coincident(g23,g20)
    c: Coincident(g23,g21)
    c: Diameter(g23) = 6.8
    c: Coincident(g2,g3)
    c: Coincident(g7,g6)
FEATURE [PartDesign::Pad] Pad010  label="Винты"
  BaseFeature = -> Pocket007
  Direction = (0,0,1)
  Length = 10.6
  Length2 = 10
  Profile = -> Sketch018
  ReferenceAxis = -> Sketch018 [N_Axis]
  Type = 0
FEATURE [Sketcher::SketchObject] Sketch019
  ExternalGeometry = -> [Pad010]
  FullyConstrained = true
  MapMode = 5
  Placement = pos=(0,0,-9) rot=(1,0,0;3.14159rad)
  Support = -> [Pad010]
  sketch-geometry (4):
    g0: Circle CenterX=-31.85 CenterY=72.5 CenterZ=0 NormalX=0 NormalY=0 NormalZ=1 AngleXU=0 Radius=3
    g1: Circle CenterX=31.85 CenterY=72.5 CenterZ=0 NormalX=0 NormalY=0 NormalZ=1 AngleXU=0 Radius=3
    g2: Circle CenterX=-31.85 CenterY=-15.5 CenterZ=0 NormalX=0 NormalY=0 NormalZ=1 AngleXU=0 Radius=3
    g3: Circle CenterX=31.85 CenterY=-15.5 CenterZ=0 NormalX=0 NormalY=0 NormalZ=1 AngleXU=0 Radius=3
  constraints (12):
    c: Diameter(g0) = 6
    c: Diameter(g1) = 6
    c: Diameter(g2) = 6
    c: Diameter(g3) = 6
    c: DistanceY(g-5,g2) = 6
    c: DistanceY(g-6,g3) = 6
    c: DistanceY(g0,g-3) = 6
    c: DistanceY(g1,g-4) = 6
    c: DistanceX(g1,g-4) = 5.85
    c: DistanceX(g-3,g0) = 5.85
    c: DistanceX(g-5,g2) = 5.85
    c: DistanceX(g3,g-6) = 5.85
FEATURE [PartDesign::Pocket] Pocket008  label="Углубления винтов"
  BaseFeature = -> Pad010
  Direction = (0,0,1)
  Length = 2.6
  Length2 = 5
  Profile = -> Sketch019
  ReferenceAxis = -> Sketch019 [N_Axis]
  Type = 0
FEATURE [PartDesign::Fillet] Fillet006  label="Сглаж: внутр боковые верх"
  Base = -> Pocket008 [Edge105,Edge125]
  BaseFeature = -> Pocket008
  Radius = 1
  SupportTransform = false
  UseAllEdges = false
FEATURE [PartDesign::Fillet] Fillet007  label="Сглаж: внутр боковые низ"
  Base = -> Fillet006 [Edge177,Edge175]
  BaseFeature = -> Fillet006
  Radius = 6
  SupportTransform = false
  UseAllEdges = false
FEATURE [PartDesign::Fillet] Fillet008  label="Сглаж: внеш боковые верх"
  Base = -> Fillet007 [Edge44,Edge61]
  BaseFeature = -> Fillet007
  Radius = 4
  SupportTransform = false
  UseAllEdges = false
FEATURE [PartDesign::Fillet] Fillet009  label="Сглаж: внеш боковые низ"
  Base = -> Fillet008 [Edge3,Edge26]
  BaseFeature = -> Fillet008
  Radius = 8
  SupportTransform = false
  UseAllEdges = false
FEATURE [PartDesign::Fillet] Fillet010  label="Сглаж: внеш плоскость"
  Base = -> Fillet009 [Edge1,Edge16,Edge18,Edge20,Edge21,Edge19,Edge17,Edge15]
  BaseFeature = -> Fillet009
  Radius = 2
  SupportTransform = false
  UseAllEdges = false
FEATURE [PartDesign::Body] Body004  label="down"
  Group = -> [Sketch014,Pad008,Sketch015,Pocket006,Sketch016,Pad009,Sketch017,Pocket007,Sketch018,Pad010,Sketch019,Pocket008,Fillet006,Fillet007,Fillet008,Fillet009,Fillet010]
  Origin = -> Origin091
  Placement = pos=(0,0,-2) rot=(0,0,1;0rad)
  Tip = -> Fillet010
FEATURE [Mesh::Feature] XT30F
  Placement = pos=(13.9,-13.9,15) rot=(0.707107,0,-0.707107;3.14159rad)
FEATURE [App::DocumentObjectGroup] Group
  Group = -> [rwled_ctrl_1,Micro_USB_B_Female_5Pin_SMD,Part__Feature056,Body001,Body003,XT30F,Circle]
